# Revit family: QF_ELECTROLUXPROFESSIONAL_588310_MA4JCCFOAO
name_source: partatom
category: Specialty Equipment
revit_build: Autodesk Revit 2018 (Build: 20190510_1515(x64)
units: mm (PartAtom-declared; Revit-internal decimal feet)

## family parameters
Always vertical = Yes
Cut with Voids When Loaded = No
Part Type = Normal
Room Calculation Point = No
Round Connector Dimension = Use Diameter
Shared = No
Work Plane-Based = No

## types (1)
- QF_ELECTROLUXPROFESSIONAL_588310_MA4JCCFOAO
    Apparent Power = 0 VA
    Conn Conduit = Yes
    Cycle = 0 Hz
    Description = EL.WARM CAB,2D,PAS,H2,GN,2S,600X800X450H
    Direct Waste Size = 0"
    Elec Conn Connection Height = 0 mm  [stored 0 ft]
    FL Amps = 0 A
    HP = 1.3 HP
    Manufacturer = ELECTROLUX
    Max Overcurrent Protection = 0 A
    Min Ckt Ampacity = 0 A
    Model = 588310
    Phase = 0
    Volts = 0 V
    Watts = 0 W
    Weight in Pounds = 57.3

note: [stored X ft] marks values corroborated as IEEE doubles in the binary element streams (Revit-internal decimal feet)

## geometry (parser evidence)
native form markers: Blend x30, Sweep x2
no freeform markers — native parametric forms only
